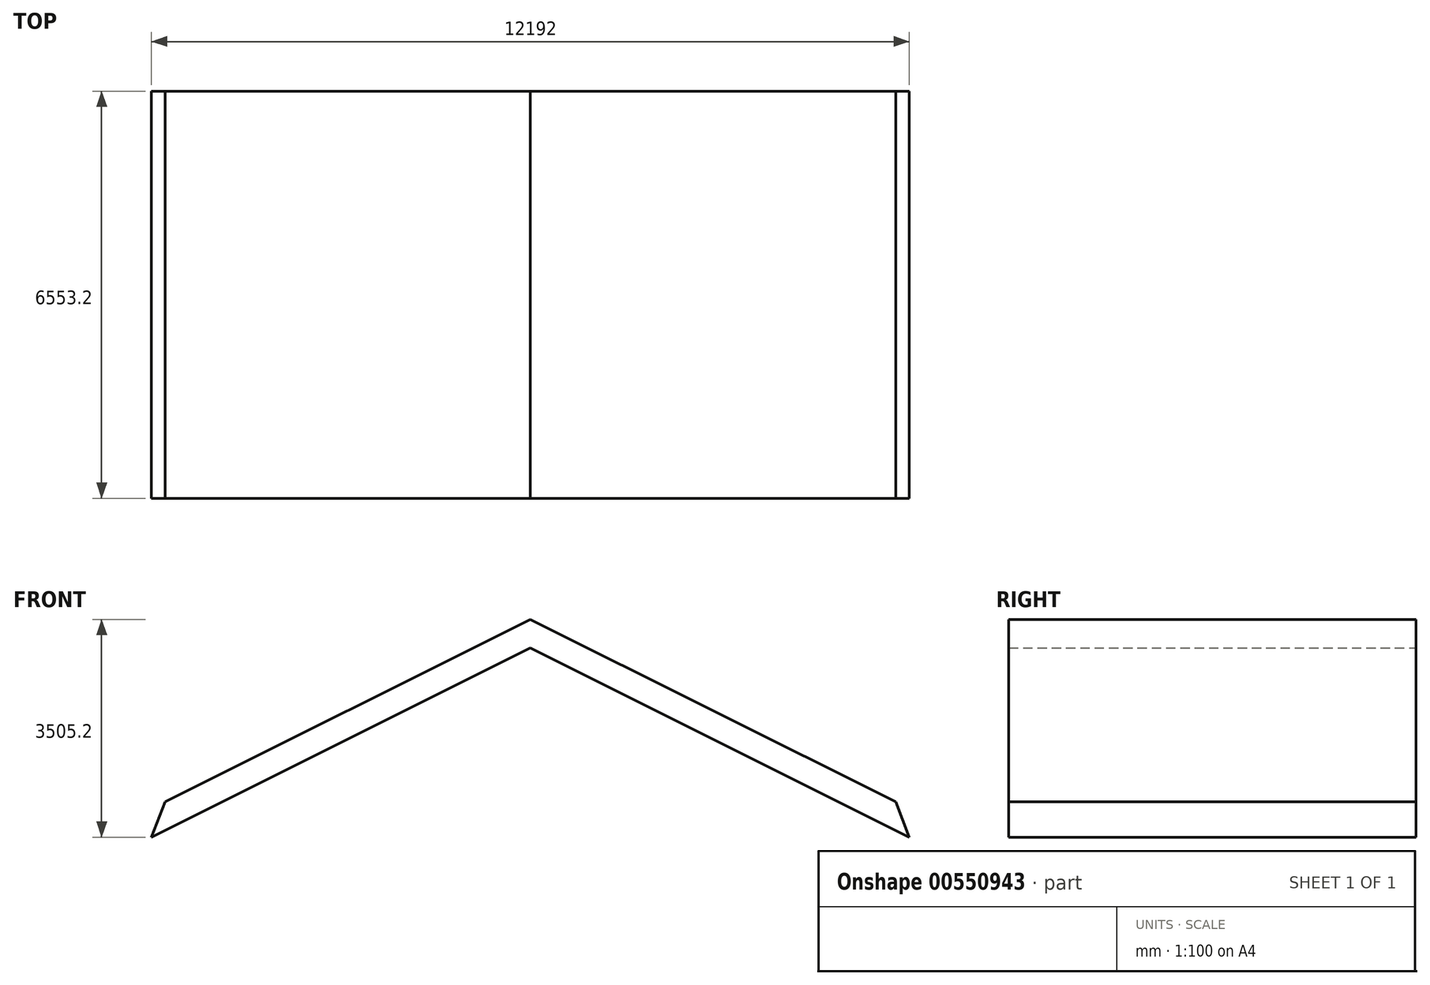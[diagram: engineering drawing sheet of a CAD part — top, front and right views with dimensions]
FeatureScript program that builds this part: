
annotation { "Feature Type Name" : "Feature", "Feature Type Description" : "" }
export const myFeature = defineFeature(function(context is Context, id is Id, definition is map)
    precondition{}
    {
        {
            var Q0;
            Q0=qCreatedBy(makeId("Front.planeOp"),FACE);
            var sketch = newSketch(context, id + "F0", { "sketchPlane" : qUnion([Q0])});
            skLineSegment(sketch, "E0", {"start": v(0, 0) * mm, "end": v(-6096, 0) * mm});
            skLineSegment(sketch, "E1", {"start": v(0, 0) * mm, "end": v(6096, 0) * mm});
            skLineSegment(sketch, "E2", {"start": v(-6096, 0) * mm, "end": v(0, 3048) * mm});
            skLineSegment(sketch, "E3", {"start": v(0, 3048) * mm, "end": v(6096, 0) * mm});
            skLineSegment(sketch, "E4", {"start": v(-6096, 0) * mm, "end": v(-6096, -7315.2) * mm});
            skLineSegment(sketch, "E5", {"start": v(-6096, -7315.2) * mm, "end": v(6096, -7315.2) * mm});
            skLineSegment(sketch, "E6", {"start": v(6096, -7315.2) * mm, "end": v(6096, 0) * mm});
            skLineSegment(sketch, "E7", {"start": v(-6096, -7315.2) * mm, "end": v(-6096, -7620) * mm});
            skLineSegment(sketch, "E8", {"start": v(6096, -7315.2) * mm, "end": v(6096, -7620) * mm});
            skLineSegment(sketch, "E9", {"start": v(-6096, -7620) * mm, "end": v(6096, -7620) * mm});
            skLineSegment(sketch, "E10", {"start": v(-304.8, -7620) * mm, "end": v(-304.8, -5486.4) * mm});
            skLineSegment(sketch, "E11", {"start": v(-304.8, -5486.4) * mm, "end": v(609.6, -5486.4) * mm});
            skLineSegment(sketch, "E12", {"start": v(609.6, -5486.4) * mm, "end": v(609.6, -7620) * mm});
            skLineSegment(sketch, "E13", {"start": v(0, 3048) * mm, "end": v(0, 3505.2) * mm});
            skLineSegment(sketch, "E14", {"start": v(0, 3505.2) * mm, "end": v(-5874.52, 567.94) * mm});
            skLineSegment(sketch, "E15", {"start": v(-5874.52, 567.94) * mm, "end": v(-6096, 0) * mm});
            skLineSegment(sketch, "E16", {"start": v(0, 3505.2) * mm, "end": v(5874.52, 567.94) * mm});
            skLineSegment(sketch, "E17", {"start": v(5874.52, 567.94) * mm, "end": v(6096, 0) * mm});
            skLineSegment(sketch, "E18", {"start": v(0, 3048) * mm, "end": v(0, 0) * mm});
            skLineSegment(sketch, "E19.bottom", {"start": v(-4572, -914.4) * mm, "end": v(-2743.2, -914.4) * mm});
            skLineSegment(sketch, "E19.top", {"start": v(-4572, -2133.6) * mm, "end": v(-2743.2, -2133.6) * mm});
            skLineSegment(sketch, "E19.left", {"start": v(-4572, -914.4) * mm, "end": v(-4572, -2133.6) * mm});
            skLineSegment(sketch, "E19.right", {"start": v(-2743.2, -914.4) * mm, "end": v(-2743.2, -2133.6) * mm});
            skLineSegment(sketch, "E20.0", {"start": v(-4876.8, -609.6) * mm, "end": v(-2438.4, -609.6) * mm});
            skLineSegment(sketch, "E20.1", {"start": v(-4876.8, -609.6) * mm, "end": v(-4876.8, -2438.4) * mm});
            skLineSegment(sketch, "E20.2", {"start": v(-4876.8, -2438.4) * mm, "end": v(-2438.4, -2438.4) * mm});
            skLineSegment(sketch, "E20.3", {"start": v(-2438.4, -609.6) * mm, "end": v(-2438.4, -2438.4) * mm});
            skLineSegment(sketch, "E21.bottom", {"start": v(2743.2, -914.4) * mm, "end": v(4572, -914.4) * mm});
            skLineSegment(sketch, "E21.top", {"start": v(2743.2, -2133.6) * mm, "end": v(4572, -2133.6) * mm});
            skLineSegment(sketch, "E21.left", {"start": v(2743.2, -914.4) * mm, "end": v(2743.2, -2133.6) * mm});
            skLineSegment(sketch, "E21.right", {"start": v(4572, -914.4) * mm, "end": v(4572, -2133.6) * mm});
            skLineSegment(sketch, "E22.0", {"start": v(2438.4, -609.6) * mm, "end": v(2438.4, -2438.4) * mm});
            skLineSegment(sketch, "E22.1", {"start": v(2438.4, -609.6) * mm, "end": v(4876.8, -609.6) * mm});
            skLineSegment(sketch, "E22.2", {"start": v(4876.8, -609.6) * mm, "end": v(4876.8, -2438.4) * mm});
            skLineSegment(sketch, "E22.3", {"start": v(2438.4, -2438.4) * mm, "end": v(4876.8, -2438.4) * mm});
            skSolve(sketch);
        }
        {
            var Q0;
            Q0=makeQuery(id+"F0.imprint","IMPRINT",FACE,{"disambiguationData":[TD([[makeQuery(id+"F0.imprint","IMPRINT",EDGE,{"derivedFrom":sQuery(id+"F0.wireOp",EDGE,"E3")}),1.0]])]});
            var Q1;
            Q1=makeQuery(id+"F0.imprint","IMPRINT",FACE,{"disambiguationData":[TD([[makeQuery(id+"F0.imprint","IMPRINT",EDGE,{"derivedFrom":sQuery(id+"F0.wireOp",EDGE,"E2")}),1.0]])]});
            extrude(context, id + "F1", {"entities" : qUnion([Q0, Q1]), "depth" : 6553.2 * mm, "offsetDistance" : 30.48 * mm});
        }
    });
